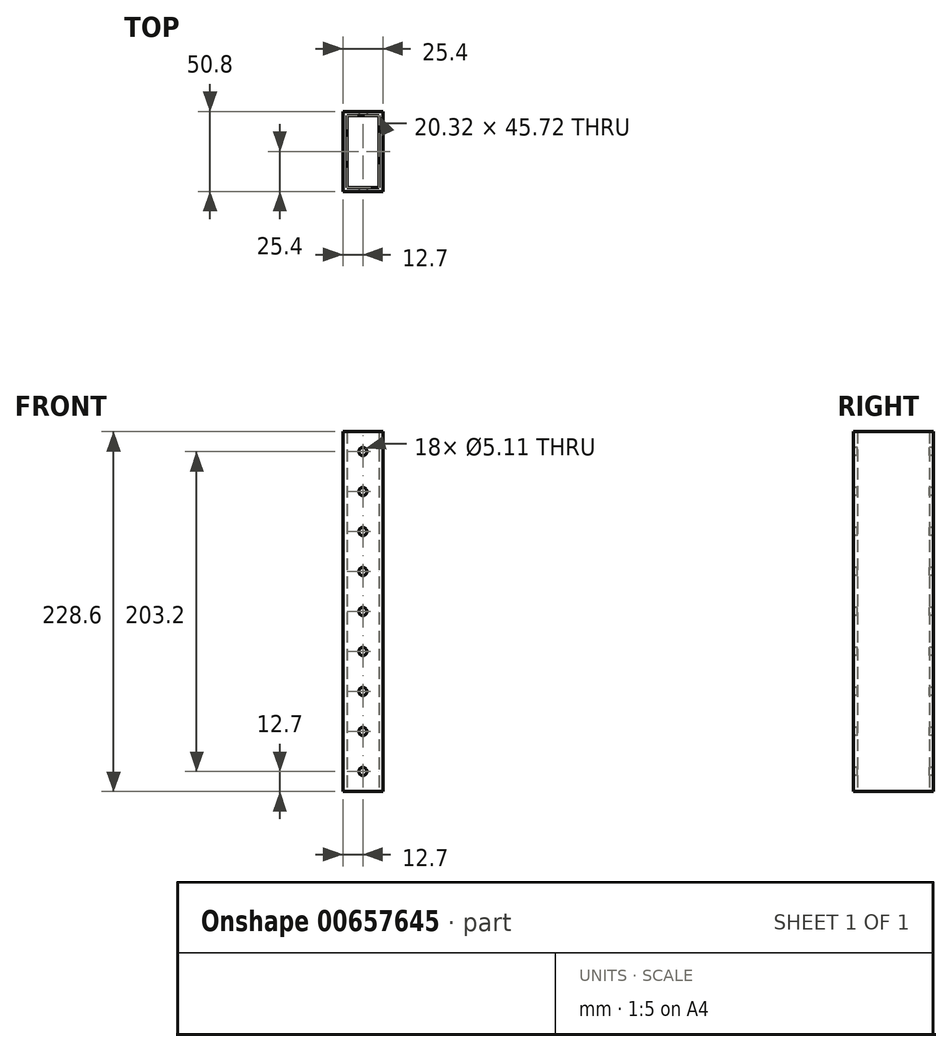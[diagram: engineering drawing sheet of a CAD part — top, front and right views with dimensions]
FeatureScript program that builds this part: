
annotation { "Feature Type Name" : "Feature", "Feature Type Description" : "" }
export const myFeature = defineFeature(function(context is Context, id is Id, definition is map)
    precondition{}
    {
        {
            var Q0;
            Q0=qCreatedBy(makeId("Top.planeOp"),FACE);
            var sketch = newSketch(context, id + "F0", { "sketchPlane" : qUnion([Q0])});
            skLineSegment(sketch, "E0.bottom", {"start": v(0, 0) * mm, "end": v(25.4, 0) * mm});
            skLineSegment(sketch, "E0.top", {"start": v(0, -50.8) * mm, "end": v(25.4, -50.8) * mm});
            skLineSegment(sketch, "E0.left", {"start": v(0, 0) * mm, "end": v(0, -50.8) * mm});
            skLineSegment(sketch, "E0.right", {"start": v(25.4, 0) * mm, "end": v(25.4, -50.8) * mm});
            skLineSegment(sketch, "E1.bottom", {"start": v(22.86, -48.26) * mm, "end": v(2.54, -48.26) * mm});
            skLineSegment(sketch, "E1.top", {"start": v(22.86, -2.54) * mm, "end": v(2.54, -2.54) * mm});
            skLineSegment(sketch, "E1.left", {"start": v(22.86, -48.26) * mm, "end": v(22.86, -2.54) * mm});
            skLineSegment(sketch, "E1.right", {"start": v(2.54, -48.26) * mm, "end": v(2.54, -2.54) * mm});
            skSolve(sketch);
        }
        {
            var Q0;
            Q0=makeQuery(id+"F0.imprint","IMPRINT",FACE,{"disambiguationData":[TD([[makeQuery(id+"F0.imprint","IMPRINT",EDGE,{"derivedFrom":sQuery(id+"F0.wireOp",EDGE,"E0.bottom")}),-1.0]])]});
            extrude(context, id + "F1", {"entities" : qUnion([Q0]), "depth" : 228.6 * mm, "offsetDistance" : 25.4 * mm});
        }
        {
            var Q0;
            Q0=makeQuery(id+"F1.opExtrude","SWEPT_FACE",FACE,{"disambiguationData":[OSD([sQuery(id+"F0.wireOp",EDGE,"E0.top")])]});
            var sketch = newSketch(context, id + "F2", { "sketchPlane" : qUnion([Q0])});
            skCircle(sketch, "E2", {"center": v(12.7, 12.7) * mm, "radius": 2.55 * mm});
            skCircle(sketch, "E3.0.1.0", {"center": v(12.7, 38.1) * mm, "radius": 2.55 * mm});
            skCircle(sketch, "E3.0.2.0", {"center": v(12.7, 63.5) * mm, "radius": 2.55 * mm});
            skCircle(sketch, "E3.0.3.0", {"center": v(12.7, 88.9) * mm, "radius": 2.55 * mm});
            skCircle(sketch, "E3.0.4.0", {"center": v(12.7, 114.3) * mm, "radius": 2.55 * mm});
            skCircle(sketch, "E3.0.5.0", {"center": v(12.7, 139.7) * mm, "radius": 2.55 * mm});
            skLineSegment(sketch, "E3.direction1", {"start": v(12.7, 12.7) * mm, "end": v(38.1, 12.7) * mm, "construction": true});
            skLineSegment(sketch, "E3.direction2", {"start": v(12.7, 12.7) * mm, "end": v(12.7, 38.1) * mm, "construction": true});
            skCircle(sketch, "E4.0.0.6", {"center": v(12.7, 165.1) * mm, "radius": 2.55 * mm});
            skCircle(sketch, "E4.0.0.7", {"center": v(12.7, 190.5) * mm, "radius": 2.55 * mm});
            skCircle(sketch, "E4.0.0.8", {"center": v(12.7, 215.9) * mm, "radius": 2.55 * mm});
            skCircle(sketch, "E5.0.0.9", {"center": v(12.7, 241.3) * mm, "radius": 2.55 * mm});
            skSolve(sketch);
        }
        {
            var Q0;
            Q0=makeQuery(id+"F2.imprint","IMPRINT",FACE,{"disambiguationData":[TD([[makeQuery(id+"F2.imprint","IMPRINT",EDGE,{"derivedFrom":sQuery(id+"F2.wireOp",EDGE,"E3.0.5.0")}),1.0]])]});
            var Q1;
            Q1=makeQuery(id+"F2.imprint","IMPRINT",FACE,{"disambiguationData":[TD([[makeQuery(id+"F2.imprint","IMPRINT",EDGE,{"derivedFrom":sQuery(id+"F2.wireOp",EDGE,"E3.0.4.0")}),1.0]])]});
            var Q2;
            Q2=makeQuery(id+"F2.imprint","IMPRINT",FACE,{"disambiguationData":[TD([[makeQuery(id+"F2.imprint","IMPRINT",EDGE,{"derivedFrom":sQuery(id+"F2.wireOp",EDGE,"E3.0.3.0")}),1.0]])]});
            var Q3;
            Q3=makeQuery(id+"F2.imprint","IMPRINT",FACE,{"disambiguationData":[TD([[makeQuery(id+"F2.imprint","IMPRINT",EDGE,{"derivedFrom":sQuery(id+"F2.wireOp",EDGE,"E3.0.2.0")}),1.0]])]});
            var Q4;
            Q4=makeQuery(id+"F2.imprint","IMPRINT",FACE,{"disambiguationData":[TD([[makeQuery(id+"F2.imprint","IMPRINT",EDGE,{"derivedFrom":sQuery(id+"F2.wireOp",EDGE,"E3.0.1.0")}),1.0]])]});
            var Q5;
            Q5=makeQuery(id+"F2.imprint","IMPRINT",FACE,{"disambiguationData":[TD([[makeQuery(id+"F2.imprint","IMPRINT",EDGE,{"derivedFrom":sQuery(id+"F2.wireOp",EDGE,"E2")}),1.0]])]});
            var Q6;
            Q6=makeQuery(id+"F2.imprint","IMPRINT",FACE,{"disambiguationData":[TD([[makeQuery(id+"F2.imprint","IMPRINT",EDGE,{"derivedFrom":sQuery(id+"F2.wireOp",EDGE,"E4.0.0.6")}),1.0]])]});
            var Q7;
            Q7=makeQuery(id+"F2.imprint","IMPRINT",FACE,{"disambiguationData":[TD([[makeQuery(id+"F2.imprint","IMPRINT",EDGE,{"derivedFrom":sQuery(id+"F2.wireOp",EDGE,"E4.0.0.7")}),1.0]])]});
            var Q8;
            Q8=makeQuery(id+"F2.imprint","IMPRINT",FACE,{"disambiguationData":[TD([[makeQuery(id+"F2.imprint","IMPRINT",EDGE,{"derivedFrom":sQuery(id+"F2.wireOp",EDGE,"E4.0.0.8")}),1.0]])]});
            var Q9;
            Q9=makeQuery(id+"F2.imprint","IMPRINT",FACE,{"disambiguationData":[TD([[makeQuery(id+"F2.imprint","IMPRINT",EDGE,{"derivedFrom":sQuery(id+"F2.wireOp",EDGE,"E5.0.0.9")}),1.0]])]});
            extrude(context, id + "F3", {"entities" : qUnion([Q0, Q1, Q2, Q3, Q4, Q5, Q6, Q7, Q8, Q9]), "operationType" : NewBodyOperationType.REMOVE, "oppositeDirection" : true, "depth" : 50.8 * mm, "offsetDistance" : 25.4 * mm});
        }
    });
